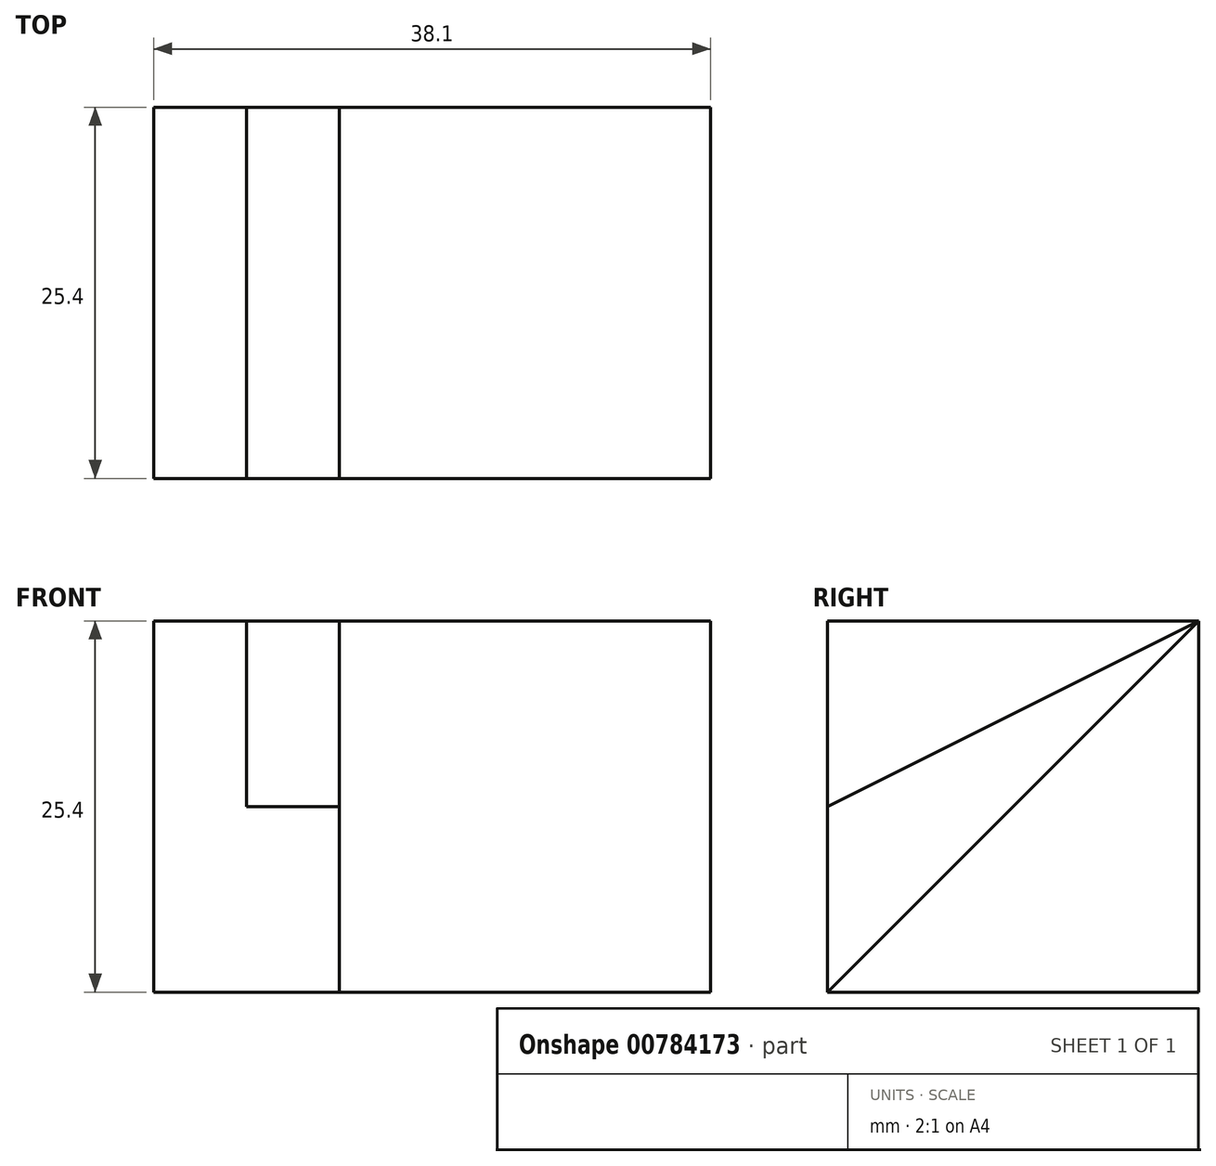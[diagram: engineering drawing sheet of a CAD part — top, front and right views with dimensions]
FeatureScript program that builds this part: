
annotation { "Feature Type Name" : "Feature", "Feature Type Description" : "" }
export const myFeature = defineFeature(function(context is Context, id is Id, definition is map)
    precondition{}
    {
        {
            var Q0;
            Q0=qCreatedBy(makeId("Front.planeOp"),FACE);
            var sketch = newSketch(context, id + "F0", { "sketchPlane" : qUnion([Q0])});
            skLineSegment(sketch, "E0", {"start": v(0, 0) * mm, "end": v(38.1, 0) * mm});
            skLineSegment(sketch, "E1", {"start": v(38.1, 0) * mm, "end": v(38.1, 25.4) * mm});
            skLineSegment(sketch, "E2", {"start": v(38.1, 25.4) * mm, "end": v(0, 25.4) * mm});
            skLineSegment(sketch, "E3", {"start": v(0, 25.4) * mm, "end": v(0, 0) * mm});
            skSolve(sketch);
        }
        {
            var Q0;
            Q0=makeQuery(id+"F0.imprint","IMPRINT",FACE,{"disambiguationData":[TD([[makeQuery(id+"F0.imprint","IMPRINT",EDGE,{"derivedFrom":sQuery(id+"F0.wireOp",EDGE,"E0")}),1.0]])]});
            extrude(context, id + "F1", {"entities" : qUnion([Q0]), "depth" : 25.4 * mm, "offsetDistance" : 25.4 * mm});
        }
        {
            var Q0;
            Q0=makeQuery(id+"F1.opExtrude","SWEPT_FACE",FACE,{"disambiguationData":[OSD([sQuery(id+"F0.wireOp",EDGE,"E1")])]});
            var sketch = newSketch(context, id + "F2", { "sketchPlane" : qUnion([Q0])});
            skLineSegment(sketch, "E4", {"start": v(0, 25.4) * mm, "end": v(-25.4, 0) * mm});
            skSolve(sketch);
        }
        {
            var Q0;
            Q0=makeQuery(id+"F2.imprint","IMPRINT",FACE,{"disambiguationData":[TD([[makeQuery(id+"F2.imprint","IMPRINT",EDGE,{"derivedFrom":sQuery(id+"F2.wireOp",EDGE,"E4")}),-1.0]])]});
            extrude(context, id + "F3", {"entities" : qUnion([Q0]), "operationType" : NewBodyOperationType.REMOVE, "oppositeDirection" : true, "depth" : 25.4 * mm, "offsetDistance" : 25.4 * mm});
        }
        {
            var Q0;
            Q0=makeQuery(id+"F3.boolean.opBoolean","COPY",FACE,{"derivedFrom":makeQuery(id+"F3.opExtrude","CAP_FACE",FACE,{"disambiguationData":[OSD([sQuery(id+"F0.wireOp",EDGE,"E1"),sQuery(id+"F0.wireOp",EDGE,"E2"),sQuery(id+"F2.wireOp",EDGE,"E4")])],"isStart":false})});
            var sketch = newSketch(context, id + "F4", { "sketchPlane" : qUnion([Q0])});
            skLineSegment(sketch, "E5", {"start": v(0, 25.4) * mm, "end": v(-25.4, 12.7) * mm});
            skSolve(sketch);
        }
        {
            var Q0;
            {var subQ0=sQuery(id+"F4.wireOp",EDGE,"E5");Q0=makeQuery(id+"F4.imprint","IMPRINT",FACE,{"disambiguationData":[TD([[makeQuery(id+"F4.imprint","IMPRINT",EDGE,{"derivedFrom":subQ0}),-1.0]])]});}
            extrude(context, id + "F5", {"entities" : qUnion([Q0]), "operationType" : NewBodyOperationType.REMOVE, "oppositeDirection" : true, "depth" : 6.35 * mm, "offsetDistance" : 25.4 * mm});
        }
    });
